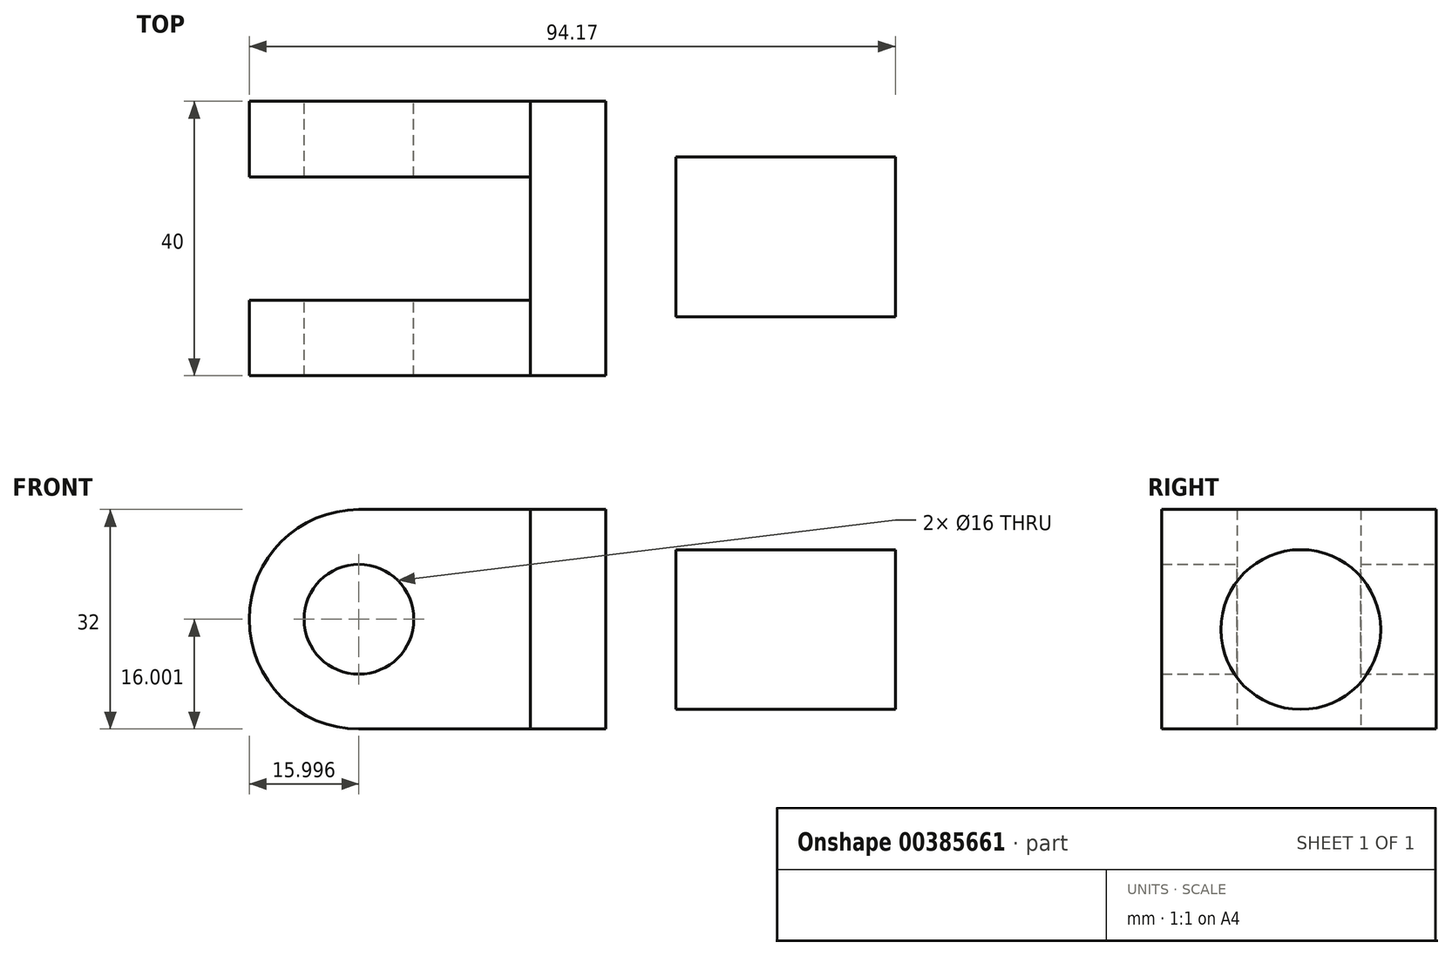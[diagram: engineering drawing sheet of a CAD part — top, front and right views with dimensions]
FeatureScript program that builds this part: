
annotation { "Feature Type Name" : "Feature", "Feature Type Description" : "" }
export const myFeature = defineFeature(function(context is Context, id is Id, definition is map)
    precondition{}
    {
        {
            var Q0;
            Q0=qCreatedBy(makeId("Front.planeOp"),FACE);
            var sketch = newSketch(context, id + "F0", { "sketchPlane" : qUnion([Q0])});
            skLineSegment(sketch, "E0", {"start": v(-46.17, -21.53) * mm, "end": v(-10.17, -21.53) * mm});
            skLineSegment(sketch, "E1", {"start": v(-10.17, -21.53) * mm, "end": v(-10.17, 10.47) * mm});
            skLineSegment(sketch, "E2", {"start": v(-10.17, 10.47) * mm, "end": v(-46.17, 10.47) * mm});
            skArc(sketch, "E3", {"start": v(-46.17, -21.53) * mm, "mid": v(-62.17, -5.53) * mm, "end": v(-46.17, 10.47) * mm});
            skCircle(sketch, "E4", {"center": v(-46.17, -5.53) * mm, "radius": 8 * mm});
            skLineSegment(sketch, "E5", {"start": v(-21.17, 10.47) * mm, "end": v(-21.17, -21.53) * mm});
            skSolve(sketch);
        }
        {
            var Q0;
            Q0=makeQuery(id+"F0.imprint","IMPRINT",FACE,{"disambiguationData":[TD([[makeQuery(id+"F0.imprint","IMPRINT",EDGE,{"derivedFrom":sQuery(id+"F0.wireOp",EDGE,"E4")}),-1.0]])]});
            extrude(context, id + "F1", {"entities" : qUnion([Q0]), "depth" : 11 * mm});
        }
        {
            var Q0;
            {var subQ0=sQuery(id+"F0.wireOp",EDGE,"E1");Q0=makeQuery(id+"F0.imprint","IMPRINT",FACE,{"disambiguationData":[TD([[makeQuery(id+"F0.imprint","IMPRINT",EDGE,{"derivedFrom":subQ0}),1.0]])]});}
            extrude(context, id + "F2", {"entities" : qUnion([Q0]), "depth" : 40 * mm});
        }
        {
            var Q0;
            Q0=makeQuery(id+"F1.opExtrude","SWEPT_BODY",BODY,{"disambiguationData":[OSD([sQuery(id+"F0.wireOp",EDGE,"E0"),sQuery(id+"F0.wireOp",EDGE,"E2"),sQuery(id+"F0.wireOp",EDGE,"E4"),sQuery(id+"F0.wireOp",EDGE,"E3"),sQuery(id+"F0.wireOp",EDGE,"E5")])]});
            transform(context, id + "F3", {"entities" : qUnion([Q0]), "transformType" : TransformType.TRANSLATION_3D, "dx" : 0 * mm, "dy" : -29 * mm, "dz" : 0 * mm, "makeCopy" : true});
        }
        {
            var Q0;
            Q0=qCreatedBy(makeId("Right.planeOp"),FACE);
            var sketch = newSketch(context, id + "F4", { "sketchPlane" : qUnion([Q0])});
            skCircle(sketch, "E6", {"center": v(-19.75, -7.02) * mm, "radius": 11.65 * mm});
            skSolve(sketch);
        }
        {
            var Q0;
            Q0=makeQuery(id+"F4.imprint","IMPRINT",FACE,{"disambiguationData":[TD([[makeQuery(id+"F4.imprint","IMPRINT",EDGE,{"derivedFrom":sQuery(id+"F4.wireOp",EDGE,"E6")}),1.0]])]});
            extrude(context, id + "F5", {"entities" : qUnion([Q0]), "depth" : 32 * mm});
        }
    });
